# Revit family: Haworth_Lyft_MotorDriven_Rectangle_Desk_EU_PRELIMINARY
name_source: partatom
category: Furniture Systems
revit_build: Autodesk Revit 2018 (Build: 20170223_1515(x64)
units: mm (PartAtom-declared; Revit-internal decimal feet)

## family parameters
Always vertical = Yes
Cut with Voids When Loaded = No
OmniClass Number = 23.40.70.14.64.21
OmniClass Title = Systems Furniture
Part Type = Normal
Room Calculation Point = No
Round Connector Dimension = Use Diameter
Shared = No
Work Plane-Based = No

## types (5) — shared parameters
Actual Height = 85 cm
Assembly Code = E2020200
Cable Finish = Haworth _ Paint _ Undecided _ Table
Cable Height = 12 cm
Cable Tray Finish = Haworth _ Polymer _ Undecided
Custom Size = No
Description = Haworth - Lyft - Motor Driven - Rectangular - Desk
Height = 85 cm
Leg Depth 80 = No
Leg Depth 90 = Yes
Leg Height = 82 cm
Manufacturer = Haworth, Inc.
Max. Depth = 90 cm
Max. Height = 130 cm
Max. Width = 200 cm
Min. Depth = 80 cm
Min. Height = 65 cm
Min. Width = 120 cm
Model = A00000001
Revision Number = 0
Size = Verify Final Dim. w/ Haworth
Standard Depths = 80, 90 cm
Standard Widths = 120, 140, 160, 180, 200 cm
Table Thickness = 3 cm
URL = https://www.haworth.com
URL - Product = https://www.haworth.com
Warranty = http://www.haworth.com

## per-type parameters (varying)
| type | Actual Depth | Actual Width | C Leg | Cable Length | Connection Width | Depth | Large | Leg Depth Back 80 | Leg Depth Back 90 | Small | T Leg | Width |
| 120w x 80d - C-Leg | 90 cm | 200 cm | Yes | 160 cm | 178 cm | 90 cm | Yes | 25 cm | 30 cm | No | No | 200 cm |
| 200w x 80d - T-Leg | 80 cm | 200 cm | No | 160 cm | 178 cm | 80 cm | No | 34 cm | 39 cm | Yes | Yes | 200 cm |
| 160w x 80d - C-Leg | 80 cm | 160 cm | Yes | 120 cm | 138 cm | 80 cm | No | 25 cm | 30 cm | Yes | No | 160 cm |
| 200w x 90d - C-Leg | 90 cm | 200 cm | Yes | 160 cm | 178 cm | 90 cm | Yes | 25 cm | 30 cm | No | No | 200 cm |
| 140w x 90d - T-Leg | 90 cm | 140 cm | No | 100 cm | 118 cm | 90 cm | Yes | 34 cm | 39 cm | No | Yes | 140 cm |

## geometry (parser evidence)
native form markers: Sweep x26
no freeform markers — native parametric forms only
